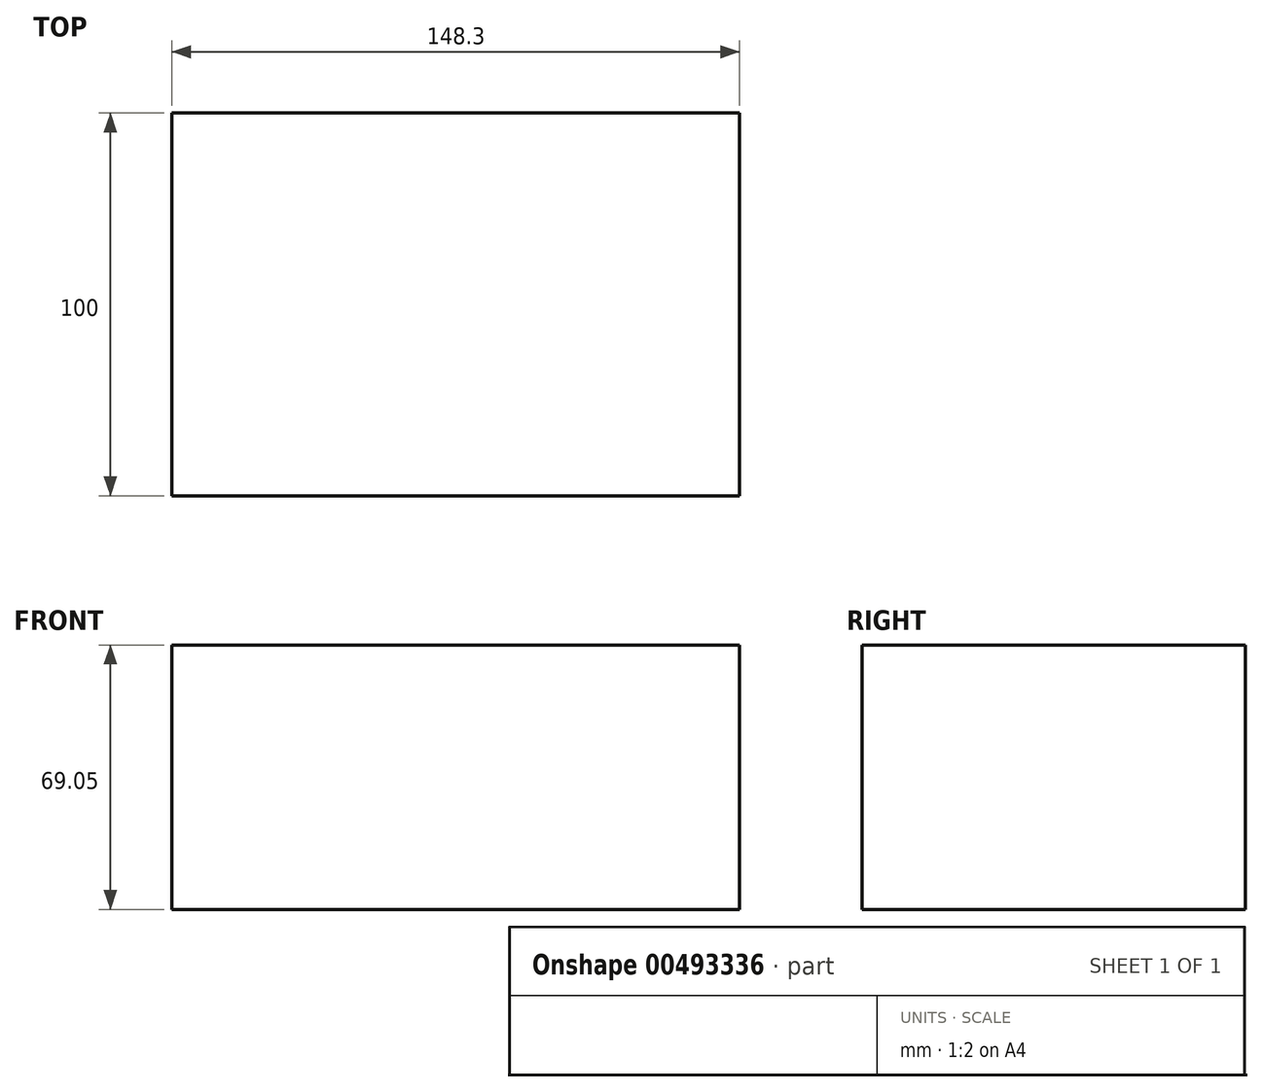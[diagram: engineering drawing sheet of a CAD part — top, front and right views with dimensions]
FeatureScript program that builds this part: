
annotation { "Feature Type Name" : "Feature", "Feature Type Description" : "" }
export const myFeature = defineFeature(function(context is Context, id is Id, definition is map)
    precondition{}
    {
        {
            var Q0;
            Q0=qCreatedBy(makeId("Front.planeOp"),FACE);
            var sketch = newSketch(context, id + "F0", { "sketchPlane" : qUnion([Q0])});
            skLineSegment(sketch, "E0.bottom", {"start": v(-90.83, 43.82) * mm, "end": v(57.47, 43.82) * mm});
            skLineSegment(sketch, "E0.top", {"start": v(-90.83, -25.23) * mm, "end": v(57.47, -25.23) * mm});
            skLineSegment(sketch, "E0.left", {"start": v(-90.83, 43.82) * mm, "end": v(-90.83, -25.23) * mm});
            skLineSegment(sketch, "E0.right", {"start": v(57.47, 43.82) * mm, "end": v(57.47, -25.23) * mm});
            skSolve(sketch);
        }
        {
            var Q0;
            Q0=makeQuery(id+"F0.imprint","IMPRINT",FACE,{"disambiguationData":[TD([[makeQuery(id+"F0.imprint","IMPRINT",EDGE,{"derivedFrom":sQuery(id+"F0.wireOp",EDGE,"E0.bottom")}),-1.0]])]});
            extrude(context, id + "F1", {"entities" : qUnion([Q0]), "depth" : 100 * mm});
        }
    });
